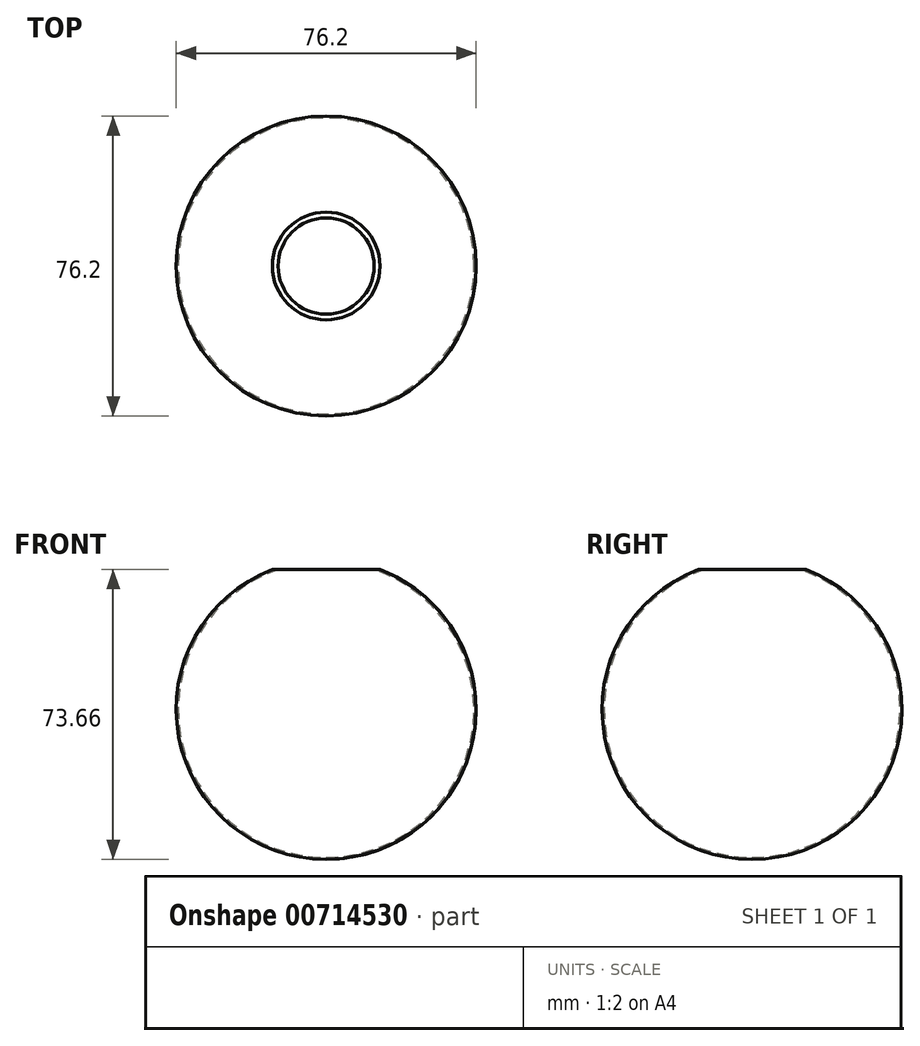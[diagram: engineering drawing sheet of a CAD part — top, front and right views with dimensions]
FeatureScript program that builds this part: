
annotation { "Feature Type Name" : "Feature", "Feature Type Description" : "" }
export const myFeature = defineFeature(function(context is Context, id is Id, definition is map)
    precondition{}
    {
        {
            var Q0;
            Q0=qCreatedBy(makeId("Front.planeOp"),FACE);
            var sketch = newSketch(context, id + "F0", { "sketchPlane" : qUnion([Q0])});
            skArc(sketch, "E0", {"start": v(0, -38.1) * mm, "mid": v(38.1, 0) * mm, "end": v(0, 38.1) * mm});
            skLineSegment(sketch, "E1", {"start": v(0, 38.1) * mm, "end": v(0, -38.1) * mm});
            skSolve(sketch);
        }
        {
            var Q0;
            Q0=makeQuery(id+"F0.imprint","IMPRINT",FACE,{"disambiguationData":[TD([[makeQuery(id+"F0.imprint","IMPRINT",EDGE,{"derivedFrom":sQuery(id+"F0.wireOp",EDGE,"E0")}),1.0]])]});
            var Q1;
            Q1=sQuery(id+"F0.wireOp",EDGE,"E1");
            revolve(context, id + "F1", {"surfaceOperationType" : NewSurfaceOperationType.NEW, "entities" : qUnion([Q0]), "axis" : qUnion([Q1]), "revolveType" : RevolveType.FULL});
        }
        {
            var Q0;
            Q0=qCreatedBy(makeId("Top.planeOp"),FACE);
            cPlane(context, id + "F2", {"entities" : qUnion([Q0]), "cplaneType" : CPlaneType.OFFSET, "offset" : 35.56 * mm, "width" : 152.4 * mm, "height" : 152.4 * mm});
        }
        {
            var Q0;
            Q0=qCreatedBy(id+"F2.planeOp",FACE);
            var sketch = newSketch(context, id + "F3", { "sketchPlane" : qUnion([Q0])});
            skLineSegment(sketch, "E2.bottom", {"start": v(-16.51, 16.51) * mm, "end": v(16.51, 16.51) * mm});
            skLineSegment(sketch, "E2.top", {"start": v(-16.51, -16.51) * mm, "end": v(16.51, -16.51) * mm});
            skLineSegment(sketch, "E2.left", {"start": v(-16.51, 16.51) * mm, "end": v(-16.51, -16.51) * mm});
            skLineSegment(sketch, "E2.right", {"start": v(16.51, 16.51) * mm, "end": v(16.51, -16.51) * mm});
            skPoint(sketch, "E2.middle", {"position": v(0, 0) * mm});
            skSolve(sketch);
        }
        {
            var Q0;
            Q0=makeQuery(id+"F3.imprint","IMPRINT",FACE,{"disambiguationData":[TD([[makeQuery(id+"F3.imprint","IMPRINT",EDGE,{"derivedFrom":sQuery(id+"F3.wireOp",EDGE,"E2.bottom")}),-1.0]])]});
            extrude(context, id + "F4", {"entities" : qUnion([Q0]), "operationType" : NewBodyOperationType.REMOVE, "depth" : 25.4 * mm, "offsetDistance" : 25.4 * mm});
        }
        {
            var Q0;
            Q0=makeQuery(id+"F4.boolean.opBoolean","COPY",FACE,{"derivedFrom":makeQuery(id+"F4.opExtrude","CAP_FACE",FACE,{"disambiguationData":[OSD([sQuery(id+"F3.wireOp",EDGE,"E2.bottom"),sQuery(id+"F3.wireOp",EDGE,"E2.top"),sQuery(id+"F3.wireOp",EDGE,"E2.left"),sQuery(id+"F3.wireOp",EDGE,"E2.right")])],"isStart":true})});
            shell(context, id + "F5", {"entities" : qUnion([Q0]), "thickness" : 0.5 * mm});
        }
    });
